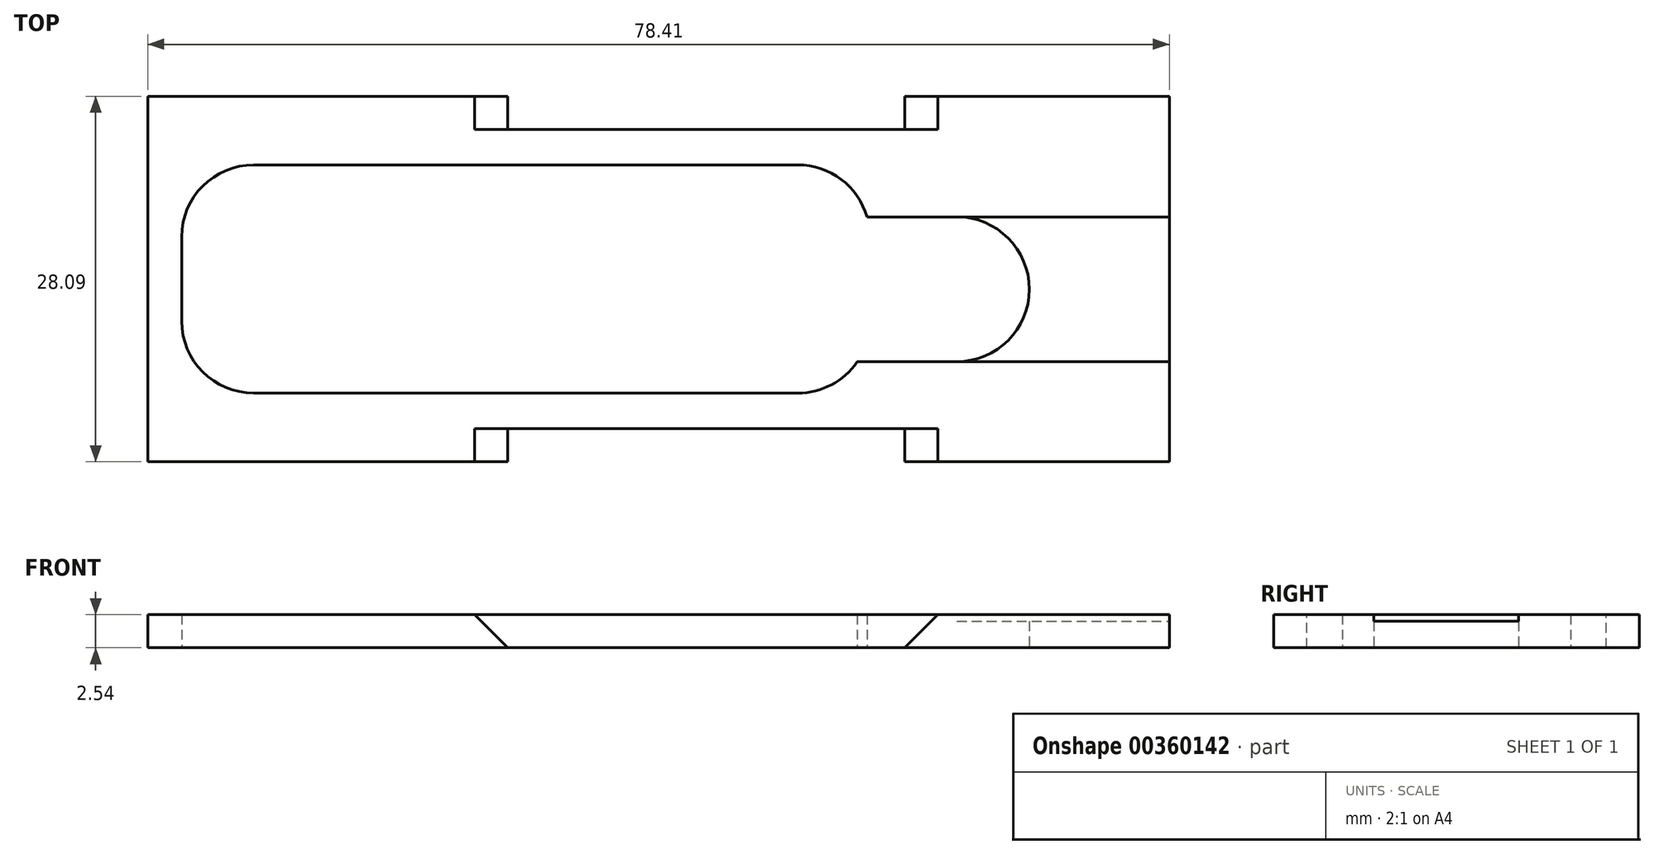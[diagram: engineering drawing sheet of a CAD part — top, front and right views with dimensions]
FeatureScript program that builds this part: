
annotation { "Feature Type Name" : "Feature", "Feature Type Description" : "" }
export const myFeature = defineFeature(function(context is Context, id is Id, definition is map)
    precondition{}
    {
        {
            var Q0;
            Q0=qCreatedBy(makeId("Top.planeOp"),FACE);
            var sketch = newSketch(context, id + "F0", { "sketchPlane" : qUnion([Q0])});
            skLineSegment(sketch, "E0.bottom", {"start": v(0, 0) * mm, "end": v(65.07, 0) * mm, "construction": true});
            skLineSegment(sketch, "E0.top", {"start": v(0, 17.53) * mm, "end": v(65.07, 17.53) * mm, "construction": true});
            skLineSegment(sketch, "E0.left", {"start": v(0, 0) * mm, "end": v(0, 17.53) * mm, "construction": true});
            skLineSegment(sketch, "E0.right", {"start": v(65.07, 0) * mm, "end": v(65.07, 17.53) * mm, "construction": true});
            skLineSegment(sketch, "E1", {"start": v(0, 5.54) * mm, "end": v(0, 11.99) * mm});
            skLineSegment(sketch, "E2", {"start": v(5.54, 17.53) * mm, "end": v(47.3, 17.53) * mm});
            skArc(sketch, "E3", {"start": v(5.54, 17.53) * mm, "mid": v(1.62, 15.9) * mm, "end": v(0, 11.99) * mm});
            skLineSegment(sketch, "E4", {"start": v(5.54, 0) * mm, "end": v(47.3, 0) * mm});
            skArc(sketch, "E5", {"start": v(0, 5.54) * mm, "mid": v(1.62, 1.62) * mm, "end": v(5.54, 0) * mm});
            skLineSegment(sketch, "E6", {"start": v(52.61, 13.54) * mm, "end": v(59.5, 13.54) * mm});
            skLineSegment(sketch, "E7", {"start": v(51.87, 2.41) * mm, "end": v(59.5, 2.41) * mm});
            skArc(sketch, "E8", {"start": v(52.61, 13.54) * mm, "mid": v(50.62, 16.42) * mm, "end": v(47.3, 17.53) * mm});
            skArc(sketch, "E9", {"start": v(47.3, 0) * mm, "mid": v(49.88, 0.64) * mm, "end": v(51.87, 2.41) * mm});
            skArc(sketch, "E10", {"start": v(59.5, 2.41) * mm, "mid": v(65.07, 7.98) * mm, "end": v(59.5, 13.54) * mm});
            skLineSegment(sketch, "E11.bottom", {"start": v(-2.6, -2.74) * mm, "end": v(75.82, -2.74) * mm});
            skLineSegment(sketch, "E11.top", {"start": v(-2.6, 20.27) * mm, "end": v(75.82, 20.27) * mm});
            skLineSegment(sketch, "E11.left", {"start": v(-2.6, -2.74) * mm, "end": v(-2.6, 20.27) * mm});
            skLineSegment(sketch, "E11.right", {"start": v(75.82, -2.74) * mm, "end": v(75.82, 20.27) * mm});
            skLineSegment(sketch, "E12", {"start": v(59.5, 13.54) * mm, "end": v(75.82, 13.54) * mm});
            skLineSegment(sketch, "E13", {"start": v(59.5, 2.41) * mm, "end": v(75.82, 2.41) * mm});
            skSolve(sketch);
        }
        {
            var Q0;
            Q0=makeQuery(id+"F0.imprint","IMPRINT",FACE,{"disambiguationData":[TD([[makeQuery(id+"F0.imprint","IMPRINT",EDGE,{"derivedFrom":sQuery(id+"F0.wireOp",EDGE,"E1")}),1.0]])]});
            extrude(context, id + "F1", {"entities" : qUnion([Q0]), "depth" : 2.54 * mm});
        }
        {
            var Q0;
            Q0=makeQuery(id+"F1.opExtrude","SWEPT_FACE",FACE,{"disambiguationData":[OSD([sQuery(id+"F0.wireOp",EDGE,"E11.bottom")])]});
            var sketch = newSketch(context, id + "F2", { "sketchPlane" : qUnion([Q0])});
            skLineSegment(sketch, "E14", {"start": v(58.04, 0) * mm, "end": v(58.04, 2.54) * mm, "construction": true});
            skLineSegment(sketch, "E15", {"start": v(22.48, 0) * mm, "end": v(22.48, 2.54) * mm, "construction": true});
            skLineSegment(sketch, "E16", {"start": v(25.02, 0) * mm, "end": v(22.48, 2.54) * mm});
            skLineSegment(sketch, "E17", {"start": v(55.5, 0) * mm, "end": v(58.04, 2.54) * mm});
            skSolve(sketch);
        }
        {
            var Q0;
            {var subQ0=sQuery(id+"F2.wireOp",EDGE,"E15");Q0=makeQuery(id+"F2.imprint","IMPRINT",FACE,{"disambiguationData":[TD([[makeQuery(id+"F2.imprint","IMPRINT",EDGE,{"derivedFrom":subQ0}),1.0]])]});}
            var Q1;
            {var subQ0=sQuery(id+"F2.wireOp",EDGE,"E14");Q1=makeQuery(id+"F2.imprint","IMPRINT",FACE,{"disambiguationData":[TD([[makeQuery(id+"F2.imprint","IMPRINT",EDGE,{"derivedFrom":subQ0}),-1.0]])]});}
            var Q2;
            {var subQ0=sQuery(id+"F2.wireOp",EDGE,"E16");Q2=makeQuery(id+"F2.imprint","IMPRINT",FACE,{"disambiguationData":[TD([[makeQuery(id+"F2.imprint","IMPRINT",EDGE,{"derivedFrom":subQ0}),1.0]])]});}
            var Q3;
            {var subQ0=sQuery(id+"F2.wireOp",EDGE,"E17");Q3=makeQuery(id+"F2.imprint","IMPRINT",FACE,{"disambiguationData":[TD([[makeQuery(id+"F2.imprint","IMPRINT",EDGE,{"derivedFrom":subQ0}),-1.0]])]});}
            extrude(context, id + "F3", {"entities" : qUnion([Q0, Q1, Q2, Q3]), "operationType" : NewBodyOperationType.ADD, "depth" : 2.54 * mm});
        }
        {
            var Q0;
            Q0=makeQuery(id+"F1.opExtrude","SWEPT_FACE",FACE,{"disambiguationData":[OSD([sQuery(id+"F0.wireOp",EDGE,"E11.top")])]});
            var sketch = newSketch(context, id + "F4", { "sketchPlane" : qUnion([Q0])});
            skLineSegment(sketch, "E18", {"start": v(-58.04, 2.54) * mm, "end": v(-58.04, 0) * mm, "construction": true});
            skLineSegment(sketch, "E19", {"start": v(-22.48, 2.54) * mm, "end": v(-22.48, 0) * mm, "construction": true});
            skLineSegment(sketch, "E20", {"start": v(-55.5, 0) * mm, "end": v(-58.04, 2.54) * mm});
            skLineSegment(sketch, "E21", {"start": v(-25.02, 0) * mm, "end": v(-22.48, 2.54) * mm});
            skSolve(sketch);
        }
        {
            var Q0;
            {var subQ0=sQuery(id+"F4.wireOp",EDGE,"E18");Q0=makeQuery(id+"F4.imprint","IMPRINT",FACE,{"disambiguationData":[TD([[makeQuery(id+"F4.imprint","IMPRINT",EDGE,{"derivedFrom":subQ0}),-1.0]])]});}
            var Q1;
            {var subQ0=sQuery(id+"F4.wireOp",EDGE,"E19");Q1=makeQuery(id+"F4.imprint","IMPRINT",FACE,{"disambiguationData":[TD([[makeQuery(id+"F4.imprint","IMPRINT",EDGE,{"derivedFrom":subQ0}),1.0]])]});}
            var Q2;
            {var subQ0=sQuery(id+"F4.wireOp",EDGE,"E20");Q2=makeQuery(id+"F4.imprint","IMPRINT",FACE,{"disambiguationData":[TD([[makeQuery(id+"F4.imprint","IMPRINT",EDGE,{"derivedFrom":subQ0}),1.0]])]});}
            var Q3;
            {var subQ0=sQuery(id+"F4.wireOp",EDGE,"E21");Q3=makeQuery(id+"F4.imprint","IMPRINT",FACE,{"disambiguationData":[TD([[makeQuery(id+"F4.imprint","IMPRINT",EDGE,{"derivedFrom":subQ0}),-1.0]])]});}
            extrude(context, id + "F5", {"entities" : qUnion([Q0, Q1, Q2, Q3]), "operationType" : NewBodyOperationType.ADD, "depth" : 2.54 * mm});
        }
        {
            var Q0;
            Q0=makeQuery(id+"F0.imprint","IMPRINT",FACE,{"disambiguationData":[TD([[makeQuery(id+"F0.imprint","IMPRINT",EDGE,{"derivedFrom":sQuery(id+"F0.wireOp",EDGE,"E10")}),-1.0]])]});
            extrude(context, id + "F6", {"entities" : qUnion([Q0]), "operationType" : NewBodyOperationType.ADD, "depth" : 2.03 * mm});
        }
    });
